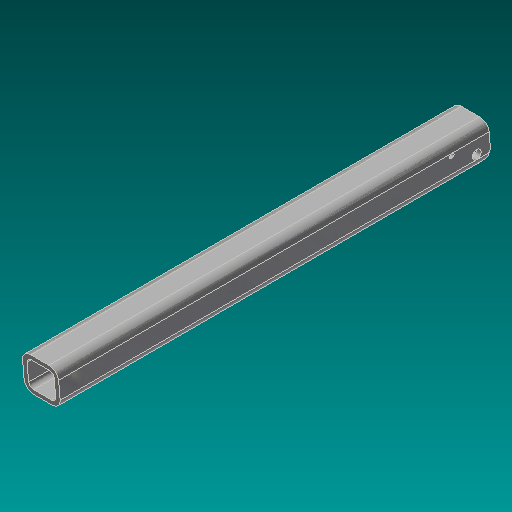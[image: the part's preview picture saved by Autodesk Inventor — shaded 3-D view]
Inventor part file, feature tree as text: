
AUTODESK INVENTOR PART (.ipt)
format: ipt  version: 2017 (Build 210142000, 142)  size: 203,776 bytes
history: native  units: mm (DEFAULTED — no unit token found)
features: sketch x5, other x3, hole x2, extrude x1, plane x1
ambient origin geometry x8: Origin, YZ Plane, XZ Plane, XY Plane, X Axis, Y Axis, Z Axis, Center Point
bodies: Solid1 (feature_tree), Body (feature_tree)
feature tree (12):
  other  "Driven Length"
  other  "Start plane"
  other  "End plane"
  extrude  "Extrusion2"  TaperAngle=0.0deg  [1 undecoded]
  hole  "Hole1"  [1 undecoded]
  hole  "Hole2"  [1 undecoded]
  sketch  "Sketch"  dims[d15=25.4mm d16=25.4mm d17=12.7mm d18=90.0deg d19=609.6mm d20=0.872665mm d21=25.4mm d22=0.0mm d23=19.05mm d24=25.4mm d25=25.4mm d26=12.7mm d27=19.05mm d28=9.525mm d29=6.35mm d30=14.3117mm d31=25.4mm d32=20.594885mm d33=53.975mm d34=9.525mm d35=6.35mm d36=19.05mm d37=9.525mm d38=6.35mm d39=14.3117mm d40=25.4mm d41=20.594885mm]
  sketch  "Sketch3"  dims[d3=609.6mm d4=0.0mm]
  plane  "Work Plane3"
  sketch  "Sketch4"  dims[d10=50.8mm d11=50.8mm]
  sketch  "Sketch5"  dims[d12=6.35mm d13=-0.0mm]
  sketch  "Sketch6"  dims[d14=609.6mm]
note: 3 required parameter values undecoded (feature->parameter linkage not recoverable at this tier; creation-order binding heuristic only, values carry confidence <= 0.55)
